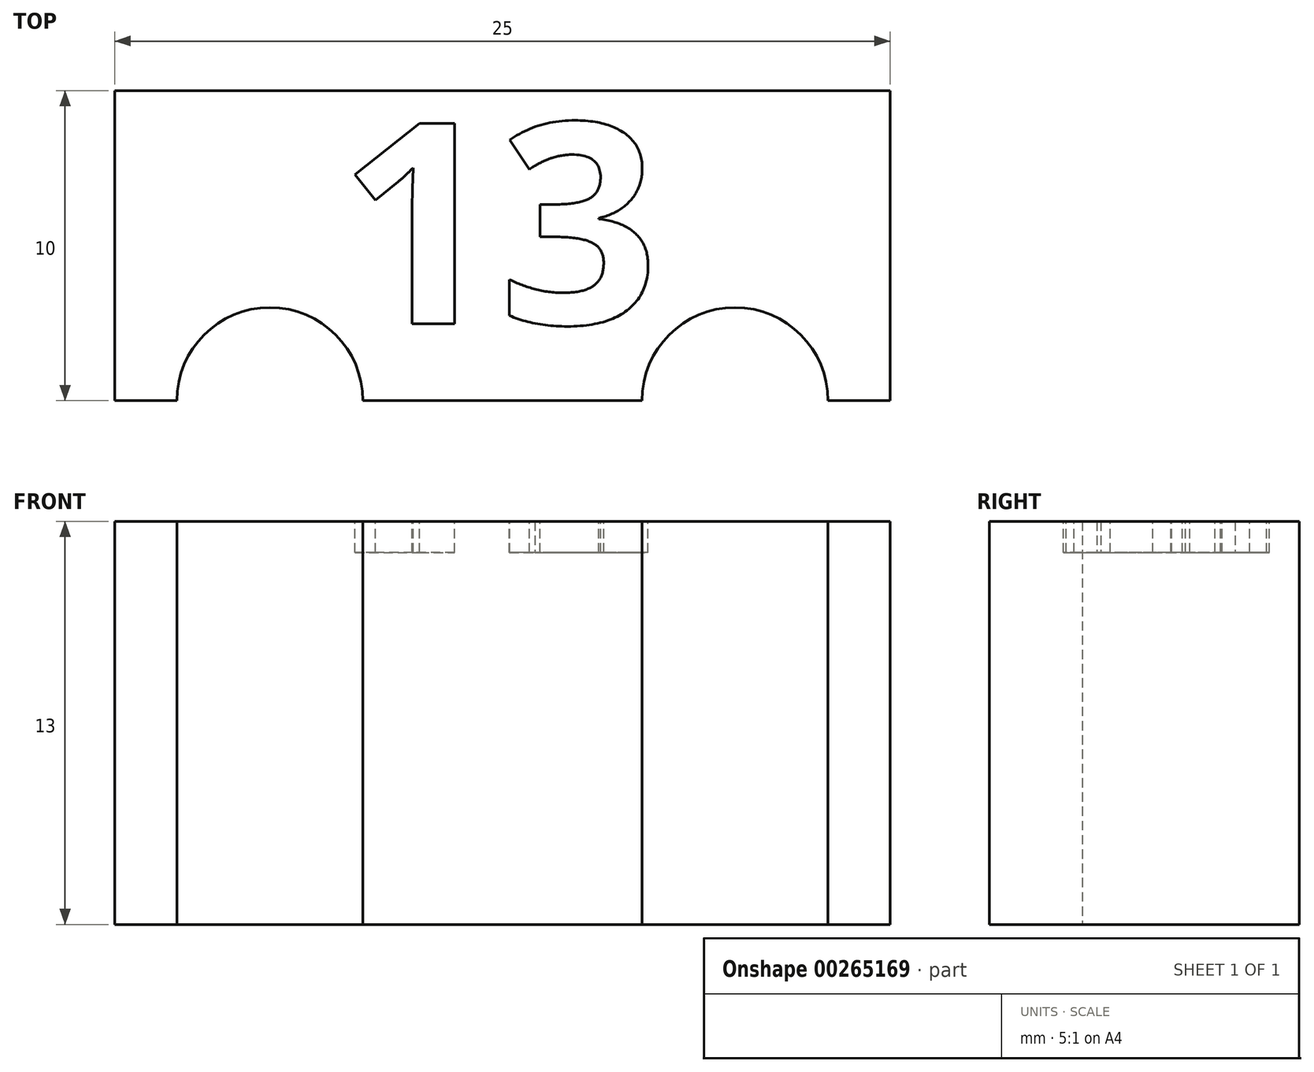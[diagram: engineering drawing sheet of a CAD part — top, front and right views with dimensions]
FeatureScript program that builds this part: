
annotation { "Feature Type Name" : "Feature", "Feature Type Description" : "" }
export const myFeature = defineFeature(function(context is Context, id is Id, definition is map)
    precondition{}
    {
        {
            var Q0;
            Q0=qCreatedBy(makeId("Top.planeOp"),FACE);
            var sketch = newSketch(context, id + "F0", { "sketchPlane" : qUnion([Q0])});
            skLineSegment(sketch, "E0.bottom", {"start": v(12.5, 5) * mm, "end": v(-12.5, 5) * mm});
            skLineSegment(sketch, "E0.top", {"start": v(12.5, -5) * mm, "end": v(-12.5, -5) * mm});
            skLineSegment(sketch, "E0.left", {"start": v(12.5, 5) * mm, "end": v(12.5, -5) * mm});
            skLineSegment(sketch, "E0.right", {"start": v(-12.5, 5) * mm, "end": v(-12.5, -5) * mm});
            skPoint(sketch, "E0.middle", {"position": v(0, 0) * mm});
            skSolve(sketch);
        }
        {
            var Q0;
            Q0 = qSketchRegion(id + "F0", true);
            extrude(context, id + "F1", {"entities" : qUnion([Q0]), "depth" : 13 * mm});
        }
        {
            var Q0;
            Q0=qCreatedBy(makeId("Top.planeOp"),FACE);
            var sketch = newSketch(context, id + "F2", { "sketchPlane" : qUnion([Q0])});
            skCircle(sketch, "E1", {"center": v(-7.5, -5) * mm, "radius": 3 * mm});
            skCircle(sketch, "E2", {"center": v(7.5, -5) * mm, "radius": 3 * mm});
            skSolve(sketch);
        }
        {
            var Q0;
            Q0 = qSketchRegion(id + "F2", true);
            extrude(context, id + "F3", {"entities" : qUnion([Q0]), "operationType" : NewBodyOperationType.REMOVE, "endBound" : BoundingType.THROUGH_ALL, "depth" : 25 * mm});
        }
        {
            var Q0;
            Q0=makeQuery(id+"F1.opExtrude","CAP_FACE",FACE,{"disambiguationData":[OSD([sQuery(id+"F0.wireOp",EDGE,"E0.bottom"),sQuery(id+"F0.wireOp",EDGE,"E0.top"),sQuery(id+"F0.wireOp",EDGE,"E0.left"),sQuery(id+"F0.wireOp",EDGE,"E0.right")])],"isStart":false});
            var sketch = newSketch(context, id + "F4", { "sketchPlane" : qUnion([Q0])});
            skText(sketch, "E3", { "text": "13", "fontName": "OpenSans-Bold.ttf"});
            skLineSegment(sketch, "E4", {"start": v(0, 4) * mm, "end": v(0, 5) * mm, "construction": true});
            const initialGuessF4  = {"E3": [-0.00529, -0.00252, 1, 0, 0.00652]};
            skSetInitialGuess(sketch, initialGuessF4);
            skSolve(sketch);
        }
        {
            var Q0;
            Q0 = qSketchRegion(id + "F4", true);
            extrude(context, id + "F5", {"entities" : qUnion([Q0]), "operationType" : NewBodyOperationType.REMOVE, "oppositeDirection" : true, "depth" : 1 * mm});
        }
    });
